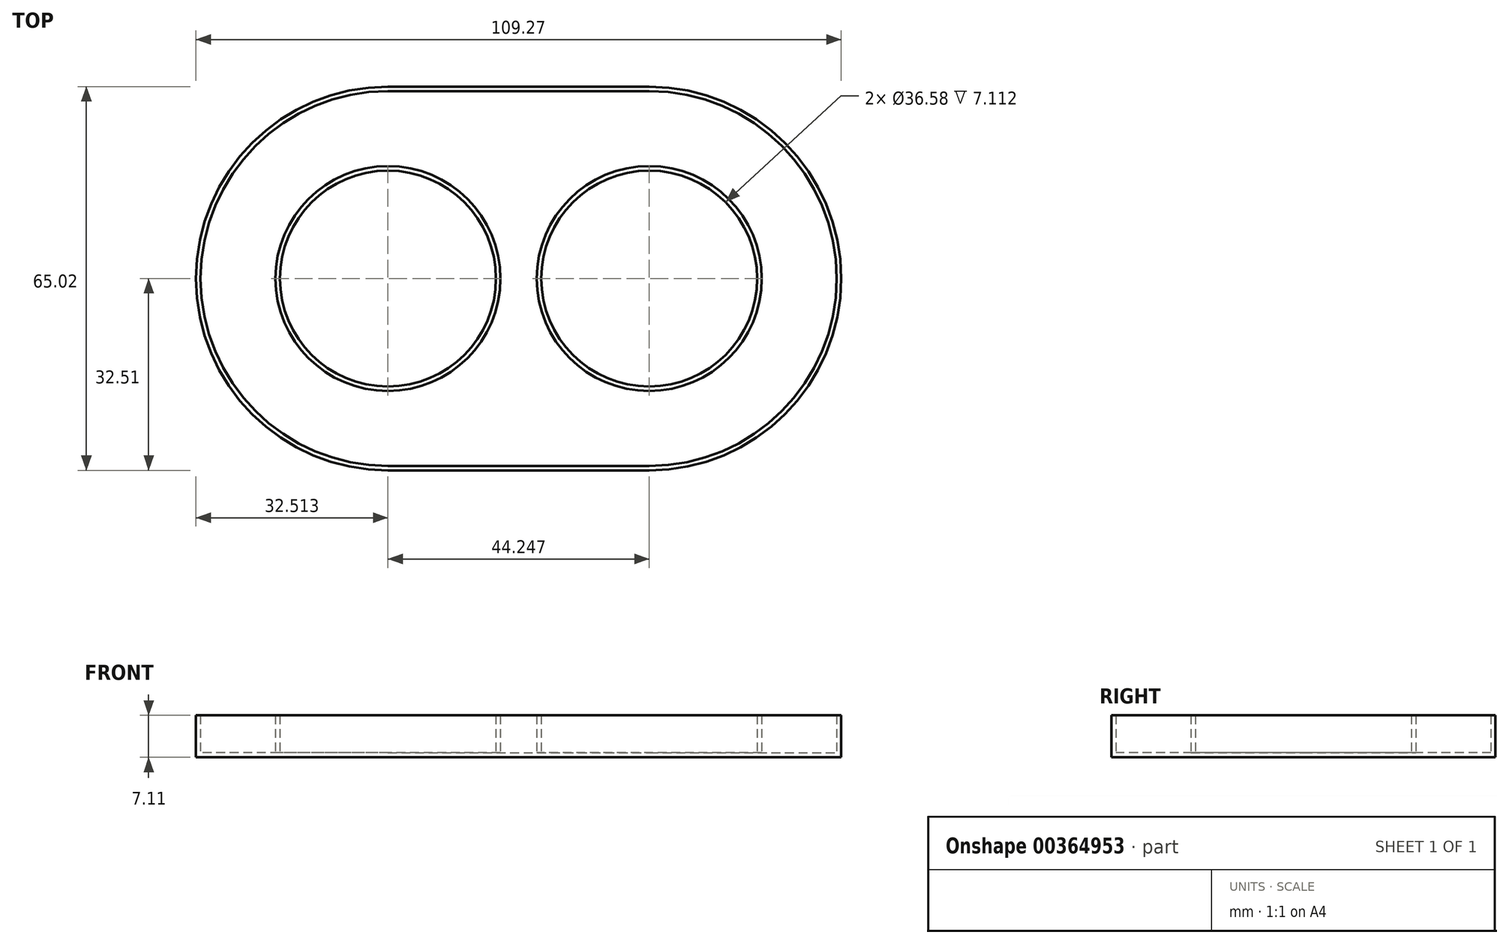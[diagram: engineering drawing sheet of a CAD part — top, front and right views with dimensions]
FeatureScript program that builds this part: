
annotation { "Feature Type Name" : "Feature", "Feature Type Description" : "" }
export const myFeature = defineFeature(function(context is Context, id is Id, definition is map)
    precondition{}
    {
        {
            var Q0;
            Q0=qCreatedBy(makeId("Top.planeOp"),FACE);
            var sketch = newSketch(context, id + "F0", { "sketchPlane" : qUnion([Q0])});
            skLineSegment(sketch, "E0", {"start": v(0, 0) * mm, "end": v(-44.25, 0) * mm, "construction": true});
            skCircle(sketch, "E1", {"center": v(-44.25, 0) * mm, "radius": 19.05 * mm});
            skCircle(sketch, "E2", {"center": v(0, 0) * mm, "radius": 19.05 * mm});
            skArc(sketch, "E3", {"start": v(-44.25, 31.75) * mm, "mid": v(-76, 0) * mm, "end": v(-44.25, -31.75) * mm});
            skLineSegment(sketch, "E4", {"start": v(-44.25, 31.75) * mm, "end": v(0, 31.75) * mm});
            skLineSegment(sketch, "E5", {"start": v(-44.25, -31.75) * mm, "end": v(0, -31.75) * mm});
            skArc(sketch, "E6.trimOffspring", {"start": v(-14.83, -11.95) * mm, "mid": v(-13.09, -6.09) * mm, "end": v(-12.5, 0) * mm});
            skArc(sketch, "E7.trimOffspring", {"start": v(0, -31.75) * mm, "mid": v(31.75, 0) * mm, "end": v(0, 31.75) * mm});
            skSolve(sketch);
        }
        {
            var Q0;
            Q0=makeQuery(id+"F0.imprint","IMPRINT",FACE,{"disambiguationData":[TD([[makeQuery(id+"F0.imprint","IMPRINT",EDGE,{"derivedFrom":sQuery(id+"F0.wireOp",EDGE,"E1")}),-1.0]])]});
            extrude(context, id + "F1", {"entities" : qUnion([Q0]), "depth" : 6.35 * mm});
        }
        {
            var Q0;
            Q0=makeQuery(id+"F1.opExtrude","CAP_FACE",FACE,{"disambiguationData":[OSD([sQuery(id+"F0.wireOp",EDGE,"E1"),sQuery(id+"F0.wireOp",EDGE,"E2"),sQuery(id+"F0.wireOp",EDGE,"E3"),sQuery(id+"F0.wireOp",EDGE,"E4"),sQuery(id+"F0.wireOp",EDGE,"E5"),sQuery(id+"F0.wireOp",EDGE,"E7.trimOffspring")])],"isStart":false});
            shell(context, id + "F2", {"entities" : qUnion([Q0]), "thickness" : 0.76 * mm, "oppositeDirection" : true});
        }
    });
